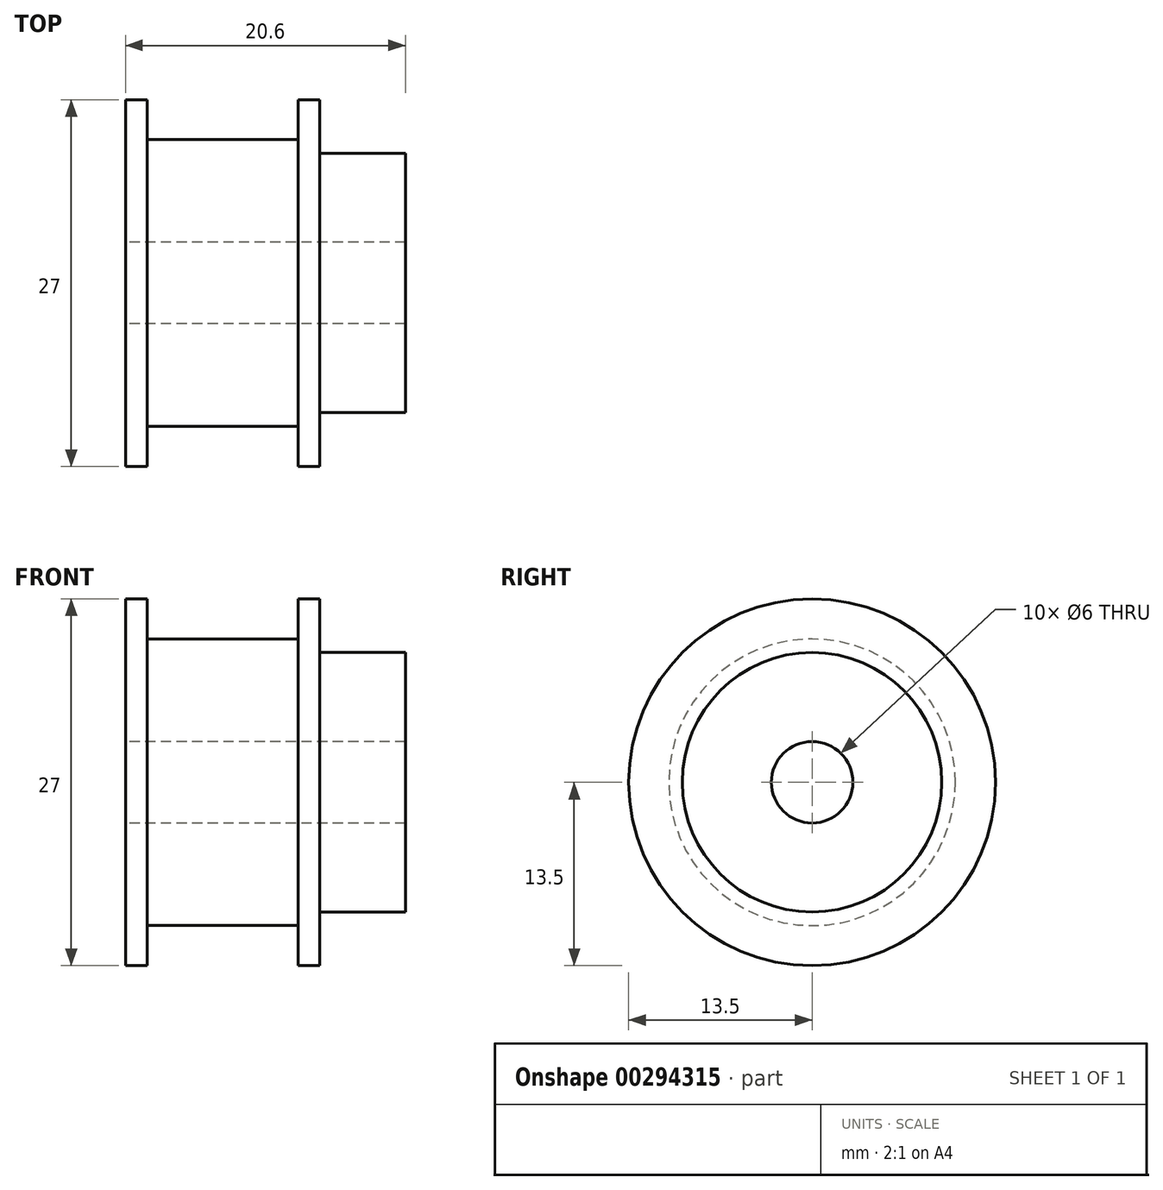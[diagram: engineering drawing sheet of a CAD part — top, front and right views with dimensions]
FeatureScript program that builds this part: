
annotation { "Feature Type Name" : "Feature", "Feature Type Description" : "" }
export const myFeature = defineFeature(function(context is Context, id is Id, definition is map)
    precondition{}
    {
        {
            var Q0;
            Q0=qCreatedBy(makeId("Front.planeOp"),FACE);
            var sketch = newSketch(context, id + "F0", { "sketchPlane" : qUnion([Q0])});
            skLineSegment(sketch, "E0", {"start": v(0, 3) * mm, "end": v(-20.6, 3) * mm});
            skLineSegment(sketch, "E1", {"start": v(-20.6, 3) * mm, "end": v(-20.6, 13.5) * mm});
            skLineSegment(sketch, "E2", {"start": v(-20.6, 13.5) * mm, "end": v(-19, 13.5) * mm});
            skLineSegment(sketch, "E3", {"start": v(-19, 13.5) * mm, "end": v(-19, 10.55) * mm});
            skLineSegment(sketch, "E4", {"start": v(-19, 10.55) * mm, "end": v(-7.9, 10.55) * mm});
            skLineSegment(sketch, "E5", {"start": v(-7.9, 10.55) * mm, "end": v(-7.9, 13.5) * mm});
            skLineSegment(sketch, "E6", {"start": v(-7.9, 13.5) * mm, "end": v(-6.3, 13.5) * mm});
            skLineSegment(sketch, "E7", {"start": v(-6.3, 13.5) * mm, "end": v(-6.3, 9.55) * mm});
            skLineSegment(sketch, "E8", {"start": v(-6.3, 9.55) * mm, "end": v(0, 9.55) * mm});
            skLineSegment(sketch, "E9", {"start": v(0, 9.55) * mm, "end": v(0, 3) * mm});
            skLineSegment(sketch, "E10", {"start": v(-26, 0) * mm, "end": v(12.31, 0) * mm, "construction": true});
            skSolve(sketch);
        }
        {
            var Q0;
            Q0 = qSketchRegion(id + "F0", true);
            var Q1;
            Q1=sQuery(id+"F0.wireOp",EDGE,"E10");
            revolve(context, id + "F1", {"entities" : qUnion([Q0]), "axis" : qUnion([Q1]), "revolveType" : RevolveType.FULL});
        }
    });
